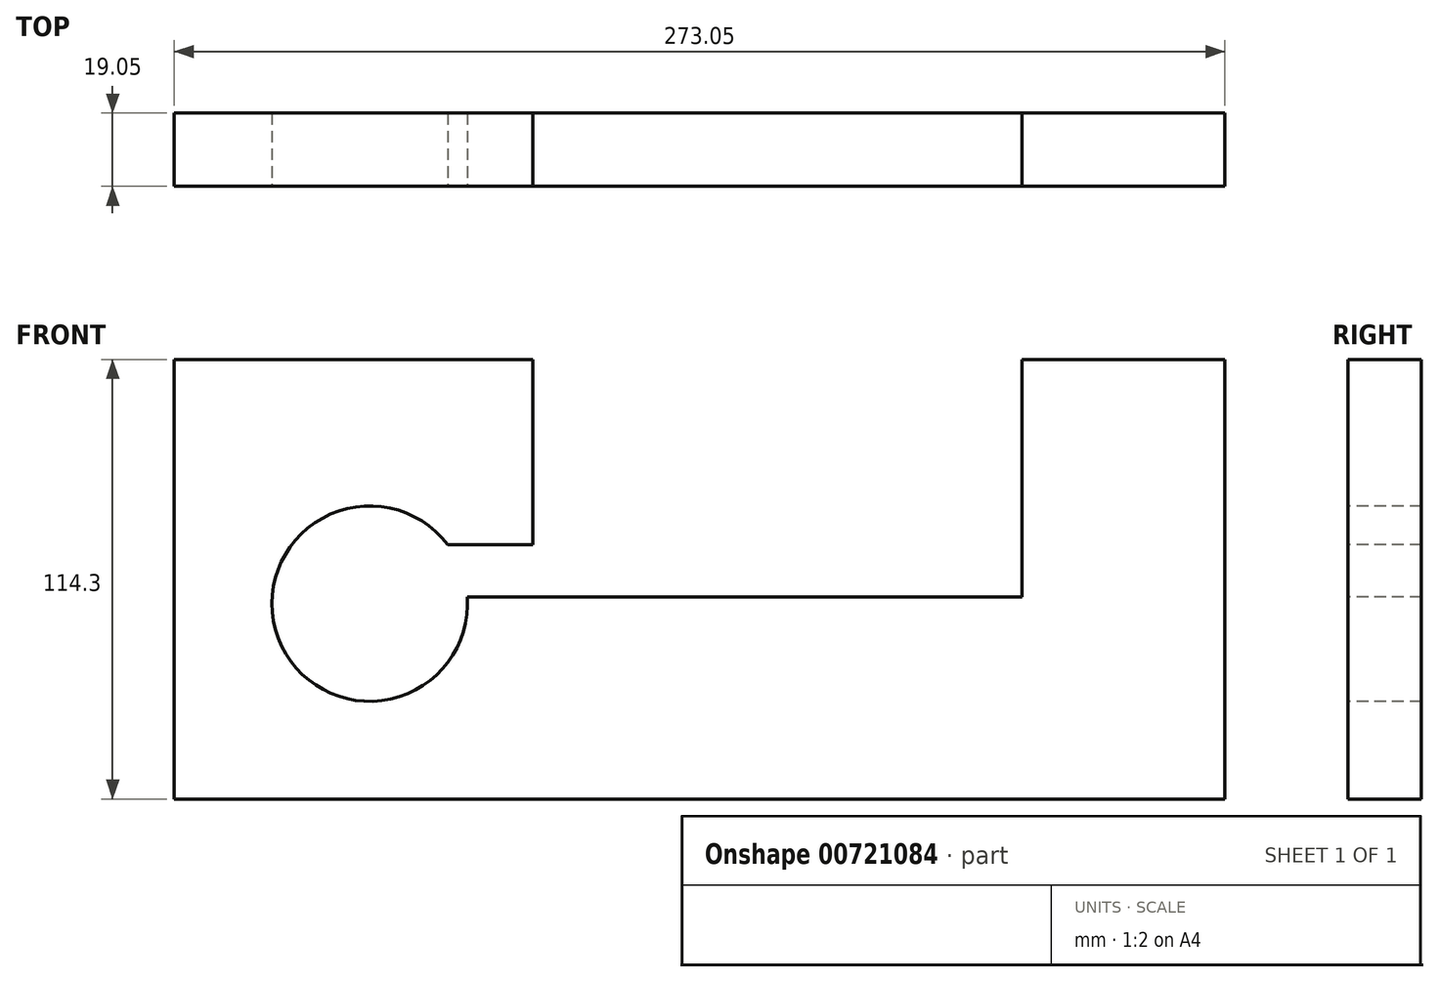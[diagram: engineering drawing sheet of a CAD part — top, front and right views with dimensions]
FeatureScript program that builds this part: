
annotation { "Feature Type Name" : "Feature", "Feature Type Description" : "" }
export const myFeature = defineFeature(function(context is Context, id is Id, definition is map)
    precondition{}
    {
        {
            var Q0;
            Q0=qCreatedBy(makeId("Front.planeOp"),FACE);
            var sketch = newSketch(context, id + "F0", { "sketchPlane" : qUnion([Q0])});
            skLineSegment(sketch, "E0.bottom", {"start": v(0, 0) * mm, "end": v(273.05, 0) * mm});
            skLineSegment(sketch, "E0.top", {"start": v(0, 114.3) * mm, "end": v(273.05, 114.3) * mm});
            skLineSegment(sketch, "E0.left", {"start": v(0, 0) * mm, "end": v(0, 114.3) * mm});
            skLineSegment(sketch, "E0.right", {"start": v(273.05, 0) * mm, "end": v(273.05, 114.3) * mm});
            skSolve(sketch);
        }
        {
            var Q0;
            Q0=qSketchRegion(id+"F0",true);
            extrude(context, id + "F1", {"entities" : qUnion([Q0]), "depth" : 19.05 * mm, "offsetDistance" : 25.4 * mm});
        }
        {
            var Q0;
            Q0=makeQuery(id+"F1.opExtrude","CAP_FACE",FACE,{"disambiguationData":[OSD([sQuery(id+"F0.wireOp",EDGE,"E0.bottom"),sQuery(id+"F0.wireOp",EDGE,"E0.top"),sQuery(id+"F0.wireOp",EDGE,"E0.left"),sQuery(id+"F0.wireOp",EDGE,"E0.right")])],"isStart":false});
            var sketch = newSketch(context, id + "F2", { "sketchPlane" : qUnion([Q0])});
            skCircle(sketch, "E1", {"center": v(50.8, 50.8) * mm, "radius": 25.4 * mm});
            skSolve(sketch);
        }
        {
            var Q0;
            Q0 = qSketchRegion(id + "F2", true);
            extrude(context, id + "F3", {"entities" : qUnion([Q0]), "operationType" : NewBodyOperationType.REMOVE, "oppositeDirection" : true, "depth" : 25.4 * mm, "offsetDistance" : 25.4 * mm});
        }
        {
            var Q0;
            Q0=makeQuery(id+"F1.opExtrude","CAP_FACE",FACE,{"disambiguationData":[OSD([sQuery(id+"F0.wireOp",EDGE,"E0.bottom"),sQuery(id+"F0.wireOp",EDGE,"E0.top"),sQuery(id+"F0.wireOp",EDGE,"E0.left"),sQuery(id+"F0.wireOp",EDGE,"E0.right")])],"isStart":false});
            var sketch = newSketch(context, id + "F4", { "sketchPlane" : qUnion([Q0])});
            skLineSegment(sketch, "E2.bottom", {"start": v(93.2, 114.3) * mm, "end": v(220.34, 114.3) * mm});
            skLineSegment(sketch, "E2.top", {"start": v(93.2, 52.58) * mm, "end": v(220.34, 52.58) * mm});
            skLineSegment(sketch, "E2.left", {"start": v(93.2, 114.3) * mm, "end": v(93.2, 52.58) * mm});
            skLineSegment(sketch, "E2.right", {"start": v(220.34, 114.3) * mm, "end": v(220.34, 52.58) * mm});
            skSolve(sketch);
        }
        {
            var Q0;
            Q0 = qSketchRegion(id + "F4", true);
            extrude(context, id + "F5", {"entities" : qUnion([Q0]), "operationType" : NewBodyOperationType.REMOVE, "oppositeDirection" : true, "depth" : 25.4 * mm, "offsetDistance" : 25.4 * mm});
        }
        {
            var Q0;
            Q0=makeQuery(id+"F1.opExtrude","CAP_FACE",FACE,{"disambiguationData":[OSD([sQuery(id+"F0.wireOp",EDGE,"E0.bottom"),sQuery(id+"F0.wireOp",EDGE,"E0.top"),sQuery(id+"F0.wireOp",EDGE,"E0.left"),sQuery(id+"F0.wireOp",EDGE,"E0.right")])],"isStart":false});
            var sketch = newSketch(context, id + "F6", { "sketchPlane" : qUnion([Q0])});
            skLineSegment(sketch, "E3", {"start": v(93.2, 66.15) * mm, "end": v(71.04, 66.15) * mm});
            skLineSegment(sketch, "E4", {"start": v(93.2, 52.58) * mm, "end": v(76.14, 52.58) * mm});
            skLineSegment(sketch, "E5", {"start": v(76.14, 52.58) * mm, "end": v(71.04, 66.15) * mm});
            skLineSegment(sketch, "E6", {"start": v(93.2, 52.58) * mm, "end": v(93.2, 66.15) * mm});
            skSolve(sketch);
        }
        {
            var Q0;
            Q0 = qSketchRegion(id + "F6", true);
            extrude(context, id + "F7", {"entities" : qUnion([Q0]), "operationType" : NewBodyOperationType.REMOVE, "oppositeDirection" : true, "depth" : 25.4 * mm, "offsetDistance" : 25.4 * mm});
        }
    });
